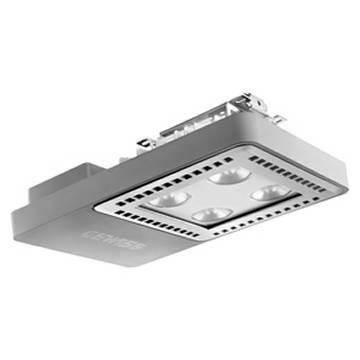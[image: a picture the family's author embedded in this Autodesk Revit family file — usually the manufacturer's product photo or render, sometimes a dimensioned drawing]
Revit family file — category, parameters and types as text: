
# Revit family: Lighting-Industriale-GEWISS-SMART[4]HLO_APPARECCHI-LED_1M_DALI
name_source: partatom
category: Apparecchi per illuminazione
units: mm (PartAtom-declared; Revit-internal decimal feet)

## family parameters
Basato su piano di lavoro = Sì
Condiviso = No
Numero OmniClass = 23.80.00.00
Punto di calcolo locali = No
Quota connettore circolare = Usa diametro
Sempre verticale = No
Sorgente d'illuminazione = No
Taglio con vuoti quando caricato = No
Tipo di parte = Normale
Titolo OmniClass = Electric Power and Lighting

## types (1)
- Lighting-Industriale-GEWISS-SMART[4]HLO_APPARECCHI-LED_1M_DALI
    Alimentatore = Incluso
    Apparecchio a ridotta temperatura superficiale = Si
    Applicazione = Interno
    Cablaggio = Con connettore stagno Gw connect
    Caratteristiche elettriche e gestione della luce = -
    Caratteristiche ottiche e illuminotecniche = -
    Carico apparente = 50 VA
    Catalogo = LIGHTING
    Certificazione DIN 18032-3 = Con Staffa - Kit Funi + morsetto (in approvazione)
    Certificazioni e classificazioni = -
    Classe fotobiologica = RG0
    Classe isolamento = I
    Classificazione = Lighting
    Classificazione: = -
    Codice Electrocod = 2444
    Codice digitale univoco (Datamatrix) = Datamatrix
    Colore = Grigio RAL 7035
    Commenti sul wattaggio = 50W
    Contesto = Illuminazione di logistiche e locali produttivi industriali
    Controllo abbagliamento e luminanza = -
    Corpo = PA6 “Halogen Free” caricato fibra vetro
    Descrizione = SMART[4]LB 1M C.PAS.DALI HLO ELL.57K
    Dispositivo di protezione = DM 6 kV / CM 10 kV
    Distanza tot_plafoniera = 74 mm  [stored 0.242782 ft]
    Durata di vita = L90B10 (Tq+25°C) = 100.000 h - L90B10 (Tq+50°C) = 50.000 h
    Efficienza luminosa (lm/W) = 128
    Finitura colore = Grigio RAL 7035
    Fissaggio = -
    Frequenza nominale (Hz) = 50/60 Hz
    Gancio di chiusura = -
    Garanzia = 5 anni
    Grado di protezione = IP66
    Gruppo ottico = Riflettore in PC metallizzato e lenti in PMMA
    Guarnizioni = tipo siliconico antinvecchiamento
    IDF = b18c6a4f-d068-432d-b6b1-00c99e93b5ad
    IDT = 0f19f0c5244441bab192072dc14552b5
    IPEA = -
    Immagine tipo = GWL1071.jpg
    Inclinazione = Con accessorio staffa
    Indice di resa cromatica = CRI-80
    Informazioni generali = -
    Installazione e manutenzione = -
    Lampada = LED
    Larghezza = 253 mm  [stored 0.830052 ft]
    Lumen output (lm) = 8200
    Lunghezza = 383 mm  [stored 1.25656 ft]
    Materiali = -
    Modello = GWS4123BQ857
    Motore = <Per categoria>
    Norma di riferimento = EN 60598-1 ; EN 60598-2-1 ; EN 60598-2-24
    Ottica = Ellittica
    Peso (kg): = 3,5
    Plafoniera = <Per categoria>
    Potenza di sistema = 64W
    Produttore = GEWISS S.p.A.
    Prospetto di default = 1219 mm
    Raggio led = 30 mm  [stored 0.0984252 ft]
    Resistenza agli urti = IK08
    Resistenza al filo incandescente = 850 °C
    SEO = Low Bay
    Scheda Tecnica = https://www.gewiss.com
    Schermo = Vetro Temprato Spessore 4mm
    Sistema di controllo = 1 x DALI DT6
    Sistema di controllo : = DALI
    Sostituibilità gruppo ottico = Non sostituibile
    Sostituibilità piastra di cablaggio = Non sostituibile
    Spessore plafoniera = 40 mm  [stored 0.131234 ft]
    Superficie massima esposta al vento : = 0,097 m²
    Temperatura di colore = 5700K
    Temperatura di esercizio = -30°C ÷ +50 °C
    Temperatura di stoccaggio = -40 +70 °C
    Tensione di alimentazione = 220 - 240 V
    Tipo di apparecchio = Riflettore industriale a LED&nbsp;
    Tipo di installazione e montaggio = Plafone - Parete - Sospensione
    Tipologia sorgente luminosa = LED - Non sostituibile
    Tolleranza cromatica = SDCM = 3
    Trasformatore = <Per categoria>
    URL = https://www.gewiss.com
    Vano di alimentazione = Integrato
    Versione file RFA = 20.11
    Vetro acceso = Lampada accesa
    Viti esterne = Acciaio inox
    Voltaggio = 230 V

note: [stored X ft] marks values corroborated as IEEE doubles in the binary element streams (Revit-internal decimal feet)

## geometry (parser evidence)
native form markers: Blend x4
no freeform markers — native parametric forms only
